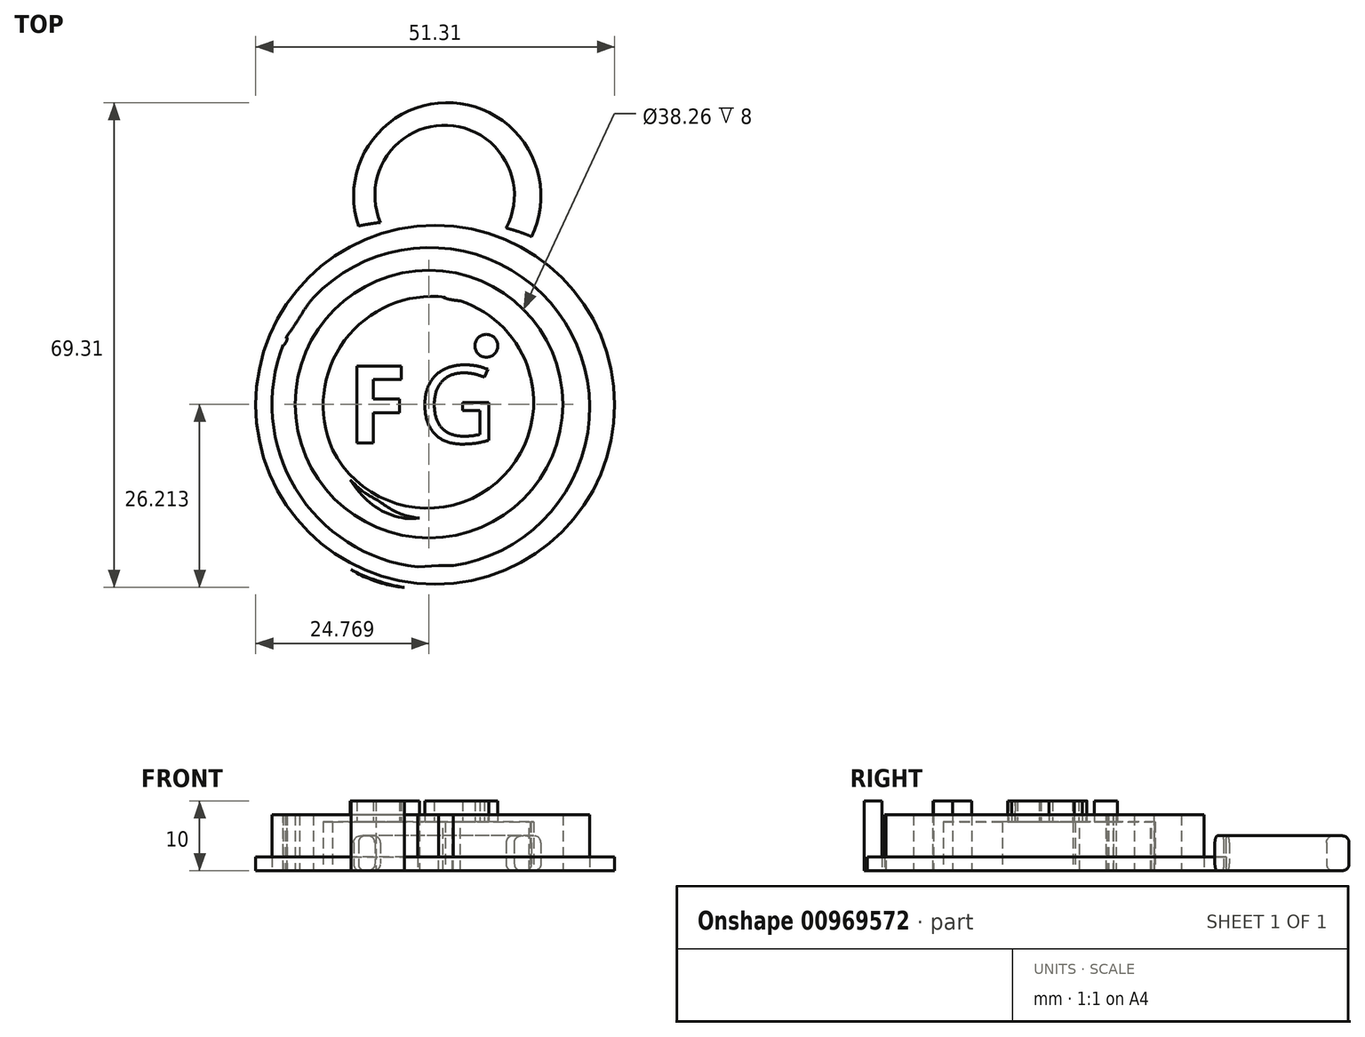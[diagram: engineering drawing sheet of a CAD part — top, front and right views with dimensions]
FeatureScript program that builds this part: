
annotation { "Feature Type Name" : "Feature", "Feature Type Description" : "" }
export const myFeature = defineFeature(function(context is Context, id is Id, definition is map)
    precondition{}
    {
        {
            var Q0;
            Q0=qCreatedBy(makeId("Top.planeOp"),FACE);
            var sketch = newSketch(context, id + "F0", { "sketchPlane" : qUnion([Q0])});
            skLineSegment(sketch, "E0", {"start": v(-44.03, -23.25) * mm, "end": v(-47.07, -23.48) * mm});
            skLineSegment(sketch, "E1", {"start": v(-47.07, -23.48) * mm, "end": v(-43.76, -23.38) * mm});
            skLineSegment(sketch, "E2", {"start": v(-0.42, -4.93) * mm, "end": v(0.75, -6.1) * mm});
            skLineSegment(sketch, "E3", {"start": v(0.75, -6.1) * mm, "end": v(0.2, -6.66) * mm});
            skLineSegment(sketch, "E4", {"start": v(0.2, -6.66) * mm, "end": v(-0.35, -7.2) * mm});
            skLineSegment(sketch, "E5", {"start": v(-0.35, -7.2) * mm, "end": v(-1.3, -6.23) * mm});
            skLineSegment(sketch, "E6", {"start": v(-5.27, -11.6) * mm, "end": v(-5.27, -10.95) * mm});
            skLineSegment(sketch, "E7", {"start": v(-5.27, -10.95) * mm, "end": v(-1.83, -10.95) * mm});
            skLineSegment(sketch, "E8", {"start": v(-1.83, -10.95) * mm, "end": v(1.61, -10.95) * mm});
            skLineSegment(sketch, "E9", {"start": v(1.61, -10.95) * mm, "end": v(1.53, -12.4) * mm});
            skLineSegment(sketch, "E10", {"start": v(34.95, -9.23) * mm, "end": v(34.95, -3.27) * mm});
            skLineSegment(sketch, "E11", {"start": v(34.95, -3.27) * mm, "end": v(35.66, -3.2) * mm});
            skLineSegment(sketch, "E12", {"start": v(35.66, -3.2) * mm, "end": v(36.37, -3.1) * mm});
            skLineSegment(sketch, "E13", {"start": v(36.37, -3.1) * mm, "end": v(36.45, -9.14) * mm});
            skLineSegment(sketch, "E14", {"start": v(44.6, -9.4) * mm, "end": v(44.74, -3.27) * mm});
            skLineSegment(sketch, "E15", {"start": v(44.74, -3.27) * mm, "end": v(45.47, -3.19) * mm});
            skLineSegment(sketch, "E16", {"start": v(45.47, -3.19) * mm, "end": v(46.2, -3.1) * mm});
            skLineSegment(sketch, "E17", {"start": v(46.2, -3.1) * mm, "end": v(46.18, -9.01) * mm});
            skLineSegment(sketch, "E18", {"start": v(4.45, -10.68) * mm, "end": v(4.52, -3.27) * mm});
            skLineSegment(sketch, "E19", {"start": v(4.52, -3.27) * mm, "end": v(5.85, -3.19) * mm});
            skLineSegment(sketch, "E20", {"start": v(9.42, -11.31) * mm, "end": v(8.63, -11.48) * mm});
            skLineSegment(sketch, "E21", {"start": v(8.63, -11.48) * mm, "end": v(11.3, -15.05) * mm});
            skLineSegment(sketch, "E22", {"start": v(11.3, -15.05) * mm, "end": v(13.95, -18.62) * mm});
            skLineSegment(sketch, "E23", {"start": v(13.95, -18.62) * mm, "end": v(13.08, -18.7) * mm});
            skLineSegment(sketch, "E24", {"start": v(5.98, -15.05) * mm, "end": v(5.98, -18.75) * mm});
            skLineSegment(sketch, "E25", {"start": v(5.98, -18.75) * mm, "end": v(5.3, -18.75) * mm});
            skLineSegment(sketch, "E26", {"start": v(7.18, -4.46) * mm, "end": v(5.98, -4.46) * mm});
            skLineSegment(sketch, "E27", {"start": v(5.98, -4.46) * mm, "end": v(5.98, -7.27) * mm});
            skLineSegment(sketch, "E28", {"start": v(5.98, -7.27) * mm, "end": v(5.98, -10.08) * mm});
            skLineSegment(sketch, "E29", {"start": v(5.98, -10.08) * mm, "end": v(7.86, -9.97) * mm});
            skLineSegment(sketch, "E30", {"start": v(49.96, -11.01) * mm, "end": v(50.03, -3.27) * mm});
            skLineSegment(sketch, "E31", {"start": v(50.03, -3.27) * mm, "end": v(51.62, -3.19) * mm});
            skLineSegment(sketch, "E32", {"start": v(52.88, -11.87) * mm, "end": v(51.49, -11.87) * mm});
            skLineSegment(sketch, "E33", {"start": v(51.49, -11.87) * mm, "end": v(51.49, -15.31) * mm});
            skLineSegment(sketch, "E34", {"start": v(51.49, -15.31) * mm, "end": v(51.49, -18.75) * mm});
            skLineSegment(sketch, "E35", {"start": v(51.49, -18.75) * mm, "end": v(50.69, -18.75) * mm});
            skLineSegment(sketch, "E36", {"start": v(50.69, -18.75) * mm, "end": v(49.9, -18.75) * mm});
            skLineSegment(sketch, "E37", {"start": v(49.9, -18.75) * mm, "end": v(49.96, -11.01) * mm});
            skLineSegment(sketch, "E38", {"start": v(52.61, -4.47) * mm, "end": v(51.49, -4.46) * mm});
            skLineSegment(sketch, "E39", {"start": v(51.49, -4.46) * mm, "end": v(51.49, -7.5) * mm});
            skLineSegment(sketch, "E40", {"start": v(-2.62, 13.4) * mm, "end": v(-2.62, 19.22) * mm});
            skLineSegment(sketch, "E41", {"start": v(-2.62, 19.22) * mm, "end": v(-1.38, 19.3) * mm});
            skLineSegment(sketch, "E42", {"start": v(-1.38, 19.3) * mm, "end": v(-0.14, 19.38) * mm});
            skLineSegment(sketch, "E43", {"start": v(-0.14, 19.38) * mm, "end": v(-0.06, 13.74) * mm});
            skLineSegment(sketch, "E44", {"start": v(7.57, 13.53) * mm, "end": v(7.7, 19.22) * mm});
            skLineSegment(sketch, "E45", {"start": v(7.7, 19.22) * mm, "end": v(8.89, 19.22) * mm});
            skLineSegment(sketch, "E46", {"start": v(8.89, 19.22) * mm, "end": v(10.08, 19.22) * mm});
            skLineSegment(sketch, "E47", {"start": v(10.08, 19.22) * mm, "end": v(10.08, 13.4) * mm});
            skLineSegment(sketch, "E48", {"start": v(1.1, 3.6) * mm, "end": v(1.1, 3.6) * mm});
            skLineSegment(sketch, "E49", {"start": v(22.7, 13.81) * mm, "end": v(22.78, 19.22) * mm});
            skLineSegment(sketch, "E50", {"start": v(22.78, 19.22) * mm, "end": v(23.97, 19.22) * mm});
            skLineSegment(sketch, "E51", {"start": v(23.97, 19.22) * mm, "end": v(25.16, 19.22) * mm});
            skLineSegment(sketch, "E52", {"start": v(25.16, 19.22) * mm, "end": v(25.3, 13.53) * mm});
            skLineSegment(sketch, "E53", {"start": v(32.92, 13.86) * mm, "end": v(33.01, 19.35) * mm});
            skLineSegment(sketch, "E54", {"start": v(33.01, 19.35) * mm, "end": v(34.18, 19.35) * mm});
            skLineSegment(sketch, "E55", {"start": v(34.18, 19.35) * mm, "end": v(35.35, 19.35) * mm});
            skLineSegment(sketch, "E56", {"start": v(35.35, 19.35) * mm, "end": v(35.35, 13.32) * mm});
            skLineSegment(sketch, "E57", {"start": v(-13.27, 11.48) * mm, "end": v(-13.2, 19.22) * mm});
            skLineSegment(sketch, "E58", {"start": v(-13.2, 19.22) * mm, "end": v(-8.97, 19.22) * mm});
            skLineSegment(sketch, "E59", {"start": v(-8.97, 19.22) * mm, "end": v(-4.74, 19.22) * mm});
            skLineSegment(sketch, "E60", {"start": v(-4.74, 19.22) * mm, "end": v(-4.66, 18.1) * mm});
            skLineSegment(sketch, "E61", {"start": v(-4.66, 18.1) * mm, "end": v(-4.57, 16.97) * mm});
            skLineSegment(sketch, "E62", {"start": v(-4.57, 16.97) * mm, "end": v(-7.63, 16.97) * mm});
            skLineSegment(sketch, "E63", {"start": v(-7.63, 16.97) * mm, "end": v(-10.69, 16.97) * mm});
            skLineSegment(sketch, "E64", {"start": v(-10.69, 16.97) * mm, "end": v(-10.69, 15.12) * mm});
            skLineSegment(sketch, "E65", {"start": v(-10.69, 15.12) * mm, "end": v(-10.69, 13.26) * mm});
            skLineSegment(sketch, "E66", {"start": v(-10.69, 13.26) * mm, "end": v(-7.65, 13.26) * mm});
            skLineSegment(sketch, "E67", {"start": v(-7.65, 13.26) * mm, "end": v(-4.6, 13.26) * mm});
            skLineSegment(sketch, "E68", {"start": v(-4.6, 13.26) * mm, "end": v(-4.6, 12.07) * mm});
            skLineSegment(sketch, "E69", {"start": v(-4.6, 12.07) * mm, "end": v(-4.6, 10.88) * mm});
            skLineSegment(sketch, "E70", {"start": v(-4.6, 10.88) * mm, "end": v(-7.65, 10.88) * mm});
            skLineSegment(sketch, "E71", {"start": v(-7.65, 10.88) * mm, "end": v(-10.69, 10.88) * mm});
            skLineSegment(sketch, "E72", {"start": v(-10.69, 10.88) * mm, "end": v(-10.69, 7.31) * mm});
            skLineSegment(sketch, "E73", {"start": v(-10.69, 7.31) * mm, "end": v(-10.69, 3.74) * mm});
            skLineSegment(sketch, "E74", {"start": v(-10.69, 3.74) * mm, "end": v(-12.02, 3.74) * mm});
            skLineSegment(sketch, "E75", {"start": v(-12.02, 3.74) * mm, "end": v(-13.34, 3.74) * mm});
            skLineSegment(sketch, "E76", {"start": v(-13.34, 3.74) * mm, "end": v(-13.27, 11.48) * mm});
            skLineSegment(sketch, "E77", {"start": v(14.99, 10.29) * mm, "end": v(15.01, 16.84) * mm});
            skLineSegment(sketch, "E78", {"start": v(15.01, 16.84) * mm, "end": v(13, 16.91) * mm});
            skLineSegment(sketch, "E79", {"start": v(13, 16.91) * mm, "end": v(10.98, 17) * mm});
            skLineSegment(sketch, "E80", {"start": v(10.98, 17) * mm, "end": v(11.06, 18.1) * mm});
            skLineSegment(sketch, "E81", {"start": v(11.06, 18.1) * mm, "end": v(11.14, 19.22) * mm});
            skLineSegment(sketch, "E82", {"start": v(11.14, 19.22) * mm, "end": v(16.43, 19.22) * mm});
            skLineSegment(sketch, "E83", {"start": v(16.43, 19.22) * mm, "end": v(21.72, 19.22) * mm});
            skLineSegment(sketch, "E84", {"start": v(21.72, 19.22) * mm, "end": v(21.8, 18.1) * mm});
            skLineSegment(sketch, "E85", {"start": v(21.8, 18.1) * mm, "end": v(21.88, 17) * mm});
            skLineSegment(sketch, "E86", {"start": v(21.88, 17) * mm, "end": v(19.82, 16.91) * mm});
            skLineSegment(sketch, "E87", {"start": v(19.82, 16.91) * mm, "end": v(17.75, 16.84) * mm});
            skLineSegment(sketch, "E88", {"start": v(17.75, 16.84) * mm, "end": v(17.75, 10.29) * mm});
            skLineSegment(sketch, "E89", {"start": v(17.75, 10.29) * mm, "end": v(17.75, 3.74) * mm});
            skLineSegment(sketch, "E90", {"start": v(17.75, 3.74) * mm, "end": v(16.36, 3.74) * mm});
            skLineSegment(sketch, "E91", {"start": v(16.36, 3.74) * mm, "end": v(14.96, 3.74) * mm});
            skLineSegment(sketch, "E92", {"start": v(14.96, 3.74) * mm, "end": v(14.99, 10.29) * mm});
            skLineSegment(sketch, "E93", {"start": v(38.06, 11.48) * mm, "end": v(38.13, 19.22) * mm});
            skLineSegment(sketch, "E94", {"start": v(38.13, 19.22) * mm, "end": v(41.1, 19.18) * mm});
            skLineSegment(sketch, "E95", {"start": v(44.73, 11.04) * mm, "end": v(43.66, 10.55) * mm});
            skLineSegment(sketch, "E96", {"start": v(43.66, 10.55) * mm, "end": v(46.05, 7.29) * mm});
            skLineSegment(sketch, "E97", {"start": v(63.29, 4.6) * mm, "end": v(63.67, 3.74) * mm});
            skLineSegment(sketch, "E98", {"start": v(63.67, 3.74) * mm, "end": v(62.27, 3.74) * mm});
            skLineSegment(sketch, "E99", {"start": v(62.27, 3.74) * mm, "end": v(60.88, 3.74) * mm});
            skLineSegment(sketch, "E100", {"start": v(60.88, 3.74) * mm, "end": v(60.06, 5.66) * mm});
            skLineSegment(sketch, "E101", {"start": v(60.06, 5.66) * mm, "end": v(59.24, 7.57) * mm});
            skLineSegment(sketch, "E102", {"start": v(59.24, 7.57) * mm, "end": v(56.22, 7.57) * mm});
            skLineSegment(sketch, "E103", {"start": v(56.22, 7.57) * mm, "end": v(53.2, 7.57) * mm});
            skLineSegment(sketch, "E104", {"start": v(53.2, 7.57) * mm, "end": v(52.75, 6.66) * mm});
            skLineSegment(sketch, "E105", {"start": v(51.9, 4.74) * mm, "end": v(51.5, 3.74) * mm});
            skLineSegment(sketch, "E106", {"start": v(51.5, 3.74) * mm, "end": v(48.6, 3.74) * mm});
            skLineSegment(sketch, "E107", {"start": v(48.6, 3.74) * mm, "end": v(45.7, 3.74) * mm});
            skLineSegment(sketch, "E108", {"start": v(45.7, 3.74) * mm, "end": v(43.43, 6.9) * mm});
            skLineSegment(sketch, "E109", {"start": v(40.64, 7.06) * mm, "end": v(40.64, 3.74) * mm});
            skLineSegment(sketch, "E110", {"start": v(40.64, 3.74) * mm, "end": v(39.31, 3.74) * mm});
            skLineSegment(sketch, "E111", {"start": v(39.31, 3.74) * mm, "end": v(37.99, 3.74) * mm});
            skLineSegment(sketch, "E112", {"start": v(37.99, 3.74) * mm, "end": v(38.06, 11.48) * mm});
            skLineSegment(sketch, "E113", {"start": v(42.1, 16.79) * mm, "end": v(40.77, 16.84) * mm});
            skLineSegment(sketch, "E114", {"start": v(40.77, 16.84) * mm, "end": v(40.7, 14.78) * mm});
            skLineSegment(sketch, "E115", {"start": v(40.7, 14.78) * mm, "end": v(40.62, 12.73) * mm});
            skLineSegment(sketch, "E116", {"start": v(40.62, 12.73) * mm, "end": v(41.95, 12.73) * mm});
            skFitSpline(sketch, "E117", {"points": [v(-48.97, -26.41) * mm, v(-51.63, -25.94) * mm, v(-55.3, -24.57) * mm, v(-57.59, -23.21) * mm]});
            skFitSpline(sketch, "E118", {"points": [v(-57.59, -23.21) * mm, v(-63.3, -19.81) * mm, v(-66.86, -15.56) * mm, v(-69.4, -9.15) * mm]});
            skFitSpline(sketch, "E119", {"points": [v(-69.4, -9.15) * mm, v(-71.48, -3.92) * mm, v(-71.54, 3.34) * mm, v(-69.55, 8.65) * mm]});
            skFitSpline(sketch, "E120", {"points": [v(-69.56, 8.67) * mm, v(-66.12, 17.83) * mm, v(-58.94, 24.16) * mm, v(-49.87, 26.04) * mm]});
            skFitSpline(sketch, "E121", {"points": [v(-49.86, 26.02) * mm, v(-46.19, 26.78) * mm, v(-40.37, 26.59) * mm, v(-37.07, 25.6) * mm]});
            skFitSpline(sketch, "E122", {"points": [v(-37.07, 25.6) * mm, v(-30.64, 23.67) * mm, v(-25.03, 19.32) * mm, v(-21.64, 13.64) * mm]});
            skFitSpline(sketch, "E123", {"points": [v(-21.64, 13.64) * mm, v(-17.98, 7.51) * mm, v(-16.93, 0.08) * mm, v(-18.72, -6.9) * mm]});
            skFitSpline(sketch, "E124", {"points": [v(-18.72, -6.9) * mm, v(-21.07, -16.02) * mm, v(-28.59, -23.55) * mm, v(-37.68, -25.92) * mm]});
            skFitSpline(sketch, "E125", {"points": [v(-37.68, -25.92) * mm, v(-40.2, -26.57) * mm, v(-46.51, -26.85) * mm, v(-48.97, -26.41) * mm]});
            skFitSpline(sketch, "E126", {"points": [v(-38.2, -22.63) * mm, v(-35.14, -21.72) * mm, v(-33.7, -21.08) * mm, v(-31.51, -19.6) * mm]});
            skFitSpline(sketch, "E127", {"points": [v(-31.51, -19.6) * mm, v(-26.64, -16.35) * mm, v(-23.18, -11.38) * mm, v(-21.75, -5.6) * mm]});
            skFitSpline(sketch, "E128", {"points": [v(-21.75, -5.6) * mm, v(-20.9, -2.13) * mm, v(-20.94, 2.46) * mm, v(-21.88, 5.9) * mm]});
            skFitSpline(sketch, "E129", {"points": [v(-21.88, 5.9) * mm, v(-23.68, 12.54) * mm, v(-28.15, 18.04) * mm, v(-34.12, 20.95) * mm]});
            skFitSpline(sketch, "E130", {"points": [v(-34.12, 20.95) * mm, v(-39.89, 23.76) * mm, v(-46.96, 24.05) * mm, v(-53.02, 21.71) * mm]});
            skFitSpline(sketch, "E131", {"points": [v(-53.02, 21.71) * mm, v(-57.82, 19.87) * mm, v(-62.76, 15.41) * mm, v(-65.06, 10.88) * mm]});
            skFitSpline(sketch, "E132", {"points": [v(-65.06, 10.88) * mm, v(-65.7, 9.62) * mm, v(-65.47, 9.88) * mm, v(-63.9, 12.23) * mm]});
            skFitSpline(sketch, "E133", {"points": [v(-63.9, 12.23) * mm, v(-62.4, 14.5) * mm, v(-59.48, 17.39) * mm, v(-57.14, 18.93) * mm]});
            skFitSpline(sketch, "E134", {"points": [v(-57.14, 18.93) * mm, v(-55.36, 20.11) * mm, v(-52.56, 21.26) * mm, v(-49.92, 21.9) * mm]});
            skFitSpline(sketch, "E135", {"points": [v(-49.92, 21.9) * mm, v(-47.26, 22.55) * mm, v(-42.13, 22.48) * mm, v(-39.4, 21.75) * mm]});
            skFitSpline(sketch, "E136", {"points": [v(-39.4, 21.75) * mm, v(-31.8, 19.74) * mm, v(-25.84, 14.14) * mm, v(-23.33, 6.65) * mm]});
            skFitSpline(sketch, "E137", {"points": [v(-23.33, 6.65) * mm, v(-22.52, 4.24) * mm, v(-22.49, 3.96) * mm, v(-22.48, -0.23) * mm]});
            skFitSpline(sketch, "E138", {"points": [v(-22.48, -0.23) * mm, v(-22.46, -5.24) * mm, v(-22.86, -7.13) * mm, v(-24.7, -10.8) * mm]});
            skFitSpline(sketch, "E139", {"points": [v(-24.7, -10.8) * mm, v(-28.37, -18.09) * mm, v(-35.4, -22.62) * mm, v(-44.03, -23.25) * mm]});
            skFitSpline(sketch, "E140", {"points": [v(-43.76, -23.38) * mm, v(-41.2, -23.31) * mm, v(-39.94, -23.14) * mm, v(-38.2, -22.63) * mm]});
            skFitSpline(sketch, "E141", {"points": [v(-41.15, -15.54) * mm, v(-37.63, -14.7) * mm, v(-33.69, -11.85) * mm, v(-31.89, -8.86) * mm]});
            skFitSpline(sketch, "E142", {"points": [v(-31.89, -8.86) * mm, v(-30.14, -5.94) * mm, v(-29.65, -4.17) * mm, v(-29.63, -0.63) * mm]});
            skFitSpline(sketch, "E143", {"points": [v(-29.63, -0.63) * mm, v(-29.61, 2.06) * mm, v(-29.7, 2.85) * mm, v(-30.25, 4.52) * mm]});
            skFitSpline(sketch, "E144", {"points": [v(-30.25, 4.52) * mm, v(-31.54, 8.44) * mm, v(-34.55, 11.9) * mm, v(-38.14, 13.6) * mm]});
            skFitSpline(sketch, "E145", {"points": [v(-38.14, 13.6) * mm, v(-39.89, 14.42) * mm, v(-42.23, 15.12) * mm, v(-43.1, 15.1) * mm]});
            skFitSpline(sketch, "E146", {"points": [v(-43.1, 15.1) * mm, v(-43.4, 15.08) * mm, v(-42.93, 14.9) * mm, v(-42.08, 14.7) * mm]});
            skFitSpline(sketch, "E147", {"points": [v(-42.08, 14.7) * mm, v(-36.92, 13.45) * mm, v(-32.57, 9.17) * mm, v(-30.96, 3.76) * mm]});
            skFitSpline(sketch, "E148", {"points": [v(-30.96, 3.76) * mm, v(-30.42, 1.93) * mm, v(-30.4, -1.75) * mm, v(-30.94, -3.79) * mm]});
            skFitSpline(sketch, "E149", {"points": [v(-30.94, -3.79) * mm, v(-31.46, -5.77) * mm, v(-32.89, -8.48) * mm, v(-34.25, -10.07) * mm]});
            skFitSpline(sketch, "E150", {"points": [v(-34.25, -10.07) * mm, v(-35.7, -11.76) * mm, v(-38.9, -13.86) * mm, v(-41.05, -14.52) * mm]});
            skFitSpline(sketch, "E151", {"points": [v(-41.05, -14.52) * mm, v(-47.68, -16.57) * mm, v(-53.9, -14.29) * mm, v(-58.4, -8.15) * mm]});
            skFitSpline(sketch, "E152", {"points": [v(-58.4, -8.15) * mm, v(-58.85, -7.53) * mm, v(-58.85, -7.54) * mm, v(-58.4, -8.41) * mm]});
            skFitSpline(sketch, "E153", {"points": [v(-58.4, -8.41) * mm, v(-57.6, -9.92) * mm, v(-54.78, -12.73) * mm, v(-52.99, -13.8) * mm]});
            skFitSpline(sketch, "E154", {"points": [v(-52.99, -13.8) * mm, v(-49.48, -15.88) * mm, v(-45.2, -16.5) * mm, v(-41.15, -15.54) * mm]});
            skFitSpline(sketch, "E155", {"points": [v(-65.73, 9.16) * mm, v(-65.73, 9.3) * mm, v(-65.85, 9.25) * mm, v(-65.99, 9.03) * mm]});
            skFitSpline(sketch, "E156", {"points": [v(-65.99, 9.03) * mm, v(-66.13, 8.81) * mm, v(-66.24, 8.51) * mm, v(-66.24, 8.37) * mm]});
            skFitSpline(sketch, "E157", {"points": [v(-66.24, 8.37) * mm, v(-66.24, 8.22) * mm, v(-66.13, 8.28) * mm, v(-65.99, 8.5) * mm]});
            skFitSpline(sketch, "E158", {"points": [v(-65.99, 8.5) * mm, v(-65.85, 8.72) * mm, v(-65.73, 9.02) * mm, v(-65.73, 9.16) * mm]});
            skFitSpline(sketch, "E159", {"points": [v(-7.85, -19) * mm, v(-10.55, -18.33) * mm, v(-12.78, -16.26) * mm, v(-13.5, -13.77) * mm]});
            skFitSpline(sketch, "E160", {"points": [v(-13.5, -13.77) * mm, v(-14.05, -11.9) * mm, v(-13.89, -9) * mm, v(-13.15, -7.37) * mm]});
            skFitSpline(sketch, "E161", {"points": [v(-13.15, -7.37) * mm, v(-11.9, -4.6) * mm, v(-9.18, -2.88) * mm, v(-6.04, -2.88) * mm]});
            skFitSpline(sketch, "E162", {"points": [v(-6.04, -2.88) * mm, v(-3.52, -2.88) * mm, v(-1.87, -3.48) * mm, v(-0.42, -4.93) * mm]});
            skFitSpline(sketch, "E163", {"points": [v(-1.3, -6.23) * mm, v(-2.48, -5.02) * mm, v(-3.34, -4.57) * mm, v(-4.93, -4.33) * mm]});
            skFitSpline(sketch, "E164", {"points": [v(-4.93, -4.33) * mm, v(-6.78, -4.05) * mm, v(-8.6, -4.58) * mm, v(-10, -5.82) * mm]});
            skFitSpline(sketch, "E165", {"points": [v(-10, -5.82) * mm, v(-11.52, -7.15) * mm, v(-12.15, -8.75) * mm, v(-12.13, -11.22) * mm]});
            skFitSpline(sketch, "E166", {"points": [v(-12.13, -11.22) * mm, v(-12.11, -14.87) * mm, v(-9.8, -17.42) * mm, v(-6.32, -17.65) * mm]});
            skFitSpline(sketch, "E167", {"points": [v(-6.32, -17.65) * mm, v(-4.4, -17.77) * mm, v(-3.08, -17.4) * mm, v(-1.91, -16.42) * mm]});
            skFitSpline(sketch, "E168", {"points": [v(-1.91, -16.42) * mm, v(-1.03, -15.68) * mm, v(-0.12, -13.96) * mm, v(-0.11, -13) * mm]});
            skFitSpline(sketch, "E169", {"points": [v(-0.11, -13) * mm, v(-0.1, -12.45) * mm, v(-0.22, -12.42) * mm, v(-2.69, -12.34) * mm]});
            skFitSpline(sketch, "E170", {"points": [v(-2.69, -12.34) * mm, v(-5.24, -12.27) * mm, v(-5.27, -12.26) * mm, v(-5.27, -11.6) * mm]});
            skFitSpline(sketch, "E171", {"points": [v(1.53, -12.4) * mm, v(1.39, -15.08) * mm, v(0, -17.2) * mm, v(-2.3, -18.34) * mm]});
            skFitSpline(sketch, "E172", {"points": [v(-2.3, -18.34) * mm, v(-3.85, -19.1) * mm, v(-6.31, -19.4) * mm, v(-7.85, -19) * mm]});
            skFitSpline(sketch, "E173", {"points": [v(21.57, -18.93) * mm, v(19.9, -18.46) * mm, v(18.03, -17.32) * mm, v(17.26, -16.3) * mm]});
            skFitSpline(sketch, "E174", {"points": [v(17.26, -16.3) * mm, v(15.86, -14.42) * mm, v(15.4, -13.16) * mm, v(15.39, -11.08) * mm]});
            skFitSpline(sketch, "E175", {"points": [v(15.39, -11.08) * mm, v(15.36, -7.62) * mm, v(16.98, -5.1) * mm, v(20.2, -3.6) * mm]});
            skFitSpline(sketch, "E176", {"points": [v(20.2, -3.6) * mm, v(21.7, -2.9) * mm, v(22.08, -2.83) * mm, v(23.91, -2.93) * mm]});
            skFitSpline(sketch, "E177", {"points": [v(23.91, -2.93) * mm, v(26.33, -3.06) * mm, v(27.95, -3.74) * mm, v(29.5, -5.3) * mm]});
            skFitSpline(sketch, "E178", {"points": [v(29.5, -5.3) * mm, v(33.43, -9.22) * mm, v(32.34, -15.77) * mm, v(27.36, -18.2) * mm]});
            skFitSpline(sketch, "E179", {"points": [v(27.36, -18.2) * mm, v(25.4, -19.15) * mm, v(23.3, -19.42) * mm, v(21.57, -18.93) * mm]});
            skFitSpline(sketch, "E180", {"points": [v(26.82, -16.89) * mm, v(29.99, -15.07) * mm, v(31.18, -11.15) * mm, v(29.54, -7.93) * mm]});
            skFitSpline(sketch, "E181", {"points": [v(29.54, -7.93) * mm, v(28.86, -6.6) * mm, v(26.92, -4.9) * mm, v(25.6, -4.51) * mm]});
            skFitSpline(sketch, "E182", {"points": [v(25.6, -4.51) * mm, v(23.3, -3.82) * mm, v(21.1, -4.29) * mm, v(19.31, -5.87) * mm]});
            skFitSpline(sketch, "E183", {"points": [v(19.31, -5.87) * mm, v(17.15, -7.77) * mm, v(16.4, -10.27) * mm, v(17.18, -12.96) * mm]});
            skFitSpline(sketch, "E184", {"points": [v(17.18, -12.96) * mm, v(18.05, -15.95) * mm, v(20.37, -17.66) * mm, v(23.57, -17.68) * mm]});
            skFitSpline(sketch, "E185", {"points": [v(23.57, -17.68) * mm, v(25.16, -17.69) * mm, v(25.62, -17.57) * mm, v(26.82, -16.89) * mm]});
            skFitSpline(sketch, "E186", {"points": [v(38.88, -19.04) * mm, v(37.4, -18.66) * mm, v(36.2, -17.73) * mm, v(35.56, -16.43) * mm]});
            skFitSpline(sketch, "E187", {"points": [v(35.56, -16.43) * mm, v(34.98, -15.23) * mm, v(34.95, -14.92) * mm, v(34.95, -9.23) * mm]});
            skFitSpline(sketch, "E188", {"points": [v(36.45, -9.14) * mm, v(36.53, -14.3) * mm, v(36.6, -15.3) * mm, v(37, -16.03) * mm]});
            skFitSpline(sketch, "E189", {"points": [v(37, -16.03) * mm, v(37.64, -17.2) * mm, v(38.72, -17.7) * mm, v(40.56, -17.69) * mm]});
            skFitSpline(sketch, "E190", {"points": [v(40.56, -17.69) * mm, v(42.32, -17.68) * mm, v(43.13, -17.34) * mm, v(43.92, -16.29) * mm]});
            skFitSpline(sketch, "E191", {"points": [v(43.92, -16.29) * mm, v(44.44, -15.6) * mm, v(44.49, -15.1) * mm, v(44.6, -9.4) * mm]});
            skFitSpline(sketch, "E192", {"points": [v(46.18, -9.01) * mm, v(46.17, -15.16) * mm, v(46, -16.32) * mm, v(44.96, -17.47) * mm]});
            skFitSpline(sketch, "E193", {"points": [v(44.96, -17.47) * mm, v(43.8, -18.77) * mm, v(40.82, -19.54) * mm, v(38.88, -19.04) * mm]});
            skFitSpline(sketch, "E194", {"points": [v(4.51, -18.42) * mm, v(4.44, -18.23) * mm, v(4.41, -14.75) * mm, v(4.45, -10.68) * mm]});
            skFitSpline(sketch, "E195", {"points": [v(5.85, -3.19) * mm, v(9, -2.98) * mm, v(11.26, -3.77) * mm, v(12.01, -5.33) * mm]});
            skFitSpline(sketch, "E196", {"points": [v(12.01, -5.33) * mm, v(12.5, -6.34) * mm, v(12.46, -8.46) * mm, v(11.95, -9.45) * mm]});
            skFitSpline(sketch, "E197", {"points": [v(11.95, -9.45) * mm, v(11.46, -10.4) * mm, v(10.54, -11.08) * mm, v(9.42, -11.31) * mm]});
            skFitSpline(sketch, "E198", {"points": [v(13.08, -18.7) * mm, v(12.48, -18.77) * mm, v(12.12, -18.65) * mm, v(11.87, -18.3) * mm]});
            skFitSpline(sketch, "E199", {"points": [v(11.87, -18.3) * mm, v(8.9, -14.16) * mm, v(6.68, -11.34) * mm, v(6.37, -11.34) * mm]});
            skFitSpline(sketch, "E200", {"points": [v(6.37, -11.34) * mm, v(6.04, -11.34) * mm, v(5.98, -11.98) * mm, v(5.98, -15.05) * mm]});
            skFitSpline(sketch, "E201", {"points": [v(5.3, -18.75) * mm, v(4.94, -18.75) * mm, v(4.58, -18.6) * mm, v(4.51, -18.42) * mm]});
            skFitSpline(sketch, "E202", {"points": [v(10.24, -9.25) * mm, v(10.8, -8.56) * mm, v(10.92, -6.62) * mm, v(10.46, -5.75) * mm]});
            skFitSpline(sketch, "E203", {"points": [v(10.46, -5.75) * mm, v(10.07, -5.02) * mm, v(8.64, -4.46) * mm, v(7.18, -4.46) * mm]});
            skFitSpline(sketch, "E204", {"points": [v(7.86, -9.97) * mm, v(9.44, -9.88) * mm, v(9.83, -9.77) * mm, v(10.24, -9.25) * mm]});
            skFitSpline(sketch, "E205", {"points": [v(51.62, -3.19) * mm, v(52.5, -3.14) * mm, v(53.86, -3.18) * mm, v(54.66, -3.28) * mm]});
            skFitSpline(sketch, "E206", {"points": [v(54.66, -3.28) * mm, v(55.9, -3.43) * mm, v(56.27, -3.62) * mm, v(57.1, -4.48) * mm]});
            skFitSpline(sketch, "E207", {"points": [v(57.1, -4.48) * mm, v(58.22, -5.67) * mm, v(58.58, -7.19) * mm, v(58.13, -8.86) * mm]});
            skFitSpline(sketch, "E208", {"points": [v(58.13, -8.86) * mm, v(57.6, -10.84) * mm, v(55.8, -11.87) * mm, v(52.88, -11.87) * mm]});
            skFitSpline(sketch, "E209", {"points": [v(53.99, -10.29) * mm, v(56.05, -9.95) * mm, v(56.62, -9.39) * mm, v(56.62, -7.68) * mm]});
            skFitSpline(sketch, "E210", {"points": [v(56.62, -7.68) * mm, v(56.62, -5.4) * mm, v(55.44, -4.47) * mm, v(52.61, -4.47) * mm]});
            skFitSpline(sketch, "E211", {"points": [v(51.49, -7.5) * mm, v(51.49, -10.96) * mm, v(51.28, -10.73) * mm, v(53.99, -10.29) * mm]});
            skFitSpline(sketch, "E212", {"points": [v(1.1, 3.6) * mm, v(-0.47, 4.16) * mm, v(-1.23, 4.82) * mm, v(-1.96, 6.27) * mm]});
            skFitSpline(sketch, "E213", {"points": [v(-1.96, 6.27) * mm, v(-2.6, 7.54) * mm, v(-2.62, 7.71) * mm, v(-2.62, 13.4) * mm]});
            skFitSpline(sketch, "E214", {"points": [v(-0.06, 13.74) * mm, v(0.04, 7.33) * mm, v(0.2, 6.74) * mm, v(2.07, 6) * mm]});
            skFitSpline(sketch, "E215", {"points": [v(2.07, 6) * mm, v(3.35, 5.48) * mm, v(4.12, 5.48) * mm, v(5.43, 6) * mm]});
            skFitSpline(sketch, "E216", {"points": [v(5.43, 6) * mm, v(7.32, 6.77) * mm, v(7.42, 7.1) * mm, v(7.57, 13.53) * mm]});
            skFitSpline(sketch, "E217", {"points": [v(10.08, 13.4) * mm, v(10.08, 10.2) * mm, v(9.99, 7.24) * mm, v(9.87, 6.84) * mm]});
            skFitSpline(sketch, "E218", {"points": [v(9.87, 6.84) * mm, v(9.52, 5.55) * mm, v(7.9, 4.05) * mm, v(6.43, 3.6) * mm]});
            skFitSpline(sketch, "E219", {"points": [v(6.43, 3.6) * mm, v(4.77, 3.11) * mm, v(2.48, 3.11) * mm, v(1.1, 3.6) * mm]});
            skFitSpline(sketch, "E220", {"points": [v(26.38, 3.6) * mm, v(25.74, 3.8) * mm, v(24.82, 4.36) * mm, v(24.32, 4.84) * mm]});
            skFitSpline(sketch, "E221", {"points": [v(24.32, 4.84) * mm, v(22.86, 6.26) * mm, v(22.63, 7.56) * mm, v(22.7, 13.81) * mm]});
            skFitSpline(sketch, "E222", {"points": [v(25.3, 13.53) * mm, v(25.44, 7.04) * mm, v(25.53, 6.74) * mm, v(27.56, 5.97) * mm]});
            skFitSpline(sketch, "E223", {"points": [v(27.56, 5.97) * mm, v(28.92, 5.45) * mm, v(30.36, 5.59) * mm, v(31.37, 6.33) * mm]});
            skFitSpline(sketch, "E224", {"points": [v(31.37, 6.33) * mm, v(32.7, 7.31) * mm, v(32.83, 7.96) * mm, v(32.92, 13.86) * mm]});
            skFitSpline(sketch, "E225", {"points": [v(35.35, 13.32) * mm, v(35.35, 7.6) * mm, v(35.32, 7.23) * mm, v(34.75, 6.11) * mm]});
            skFitSpline(sketch, "E226", {"points": [v(34.75, 6.11) * mm, v(34.1, 4.83) * mm, v(32.92, 3.9) * mm, v(31.41, 3.48) * mm]});
            skFitSpline(sketch, "E227", {"points": [v(31.41, 3.48) * mm, v(30.1, 3.11) * mm, v(27.78, 3.17) * mm, v(26.38, 3.6) * mm]});
            skFitSpline(sketch, "E228", {"points": [v(41.1, 19.18) * mm, v(43.46, 19.15) * mm, v(44.23, 19.04) * mm, v(44.9, 18.65) * mm]});
            skFitSpline(sketch, "E229", {"points": [v(44.9, 18.65) * mm, v(46.28, 17.84) * mm, v(46.82, 16.9) * mm, v(46.93, 15.05) * mm]});
            skFitSpline(sketch, "E230", {"points": [v(46.93, 15.05) * mm, v(47.02, 13.65) * mm, v(46.94, 13.25) * mm, v(46.42, 12.47) * mm]});
            skFitSpline(sketch, "E231", {"points": [v(46.42, 12.47) * mm, v(46.08, 11.96) * mm, v(45.32, 11.32) * mm, v(44.73, 11.04) * mm]});
            skFitSpline(sketch, "E232", {"points": [v(46.05, 7.29) * mm, v(47.37, 5.5) * mm, v(48.5, 4.03) * mm, v(48.59, 4.02) * mm]});
            skFitSpline(sketch, "E233", {"points": [v(48.59, 4.02) * mm, v(48.78, 4) * mm, v(49.77, 6.01) * mm, v(52.54, 12.07) * mm]});
            skFitSpline(sketch, "E234", {"points": [v(52.54, 12.07) * mm, v(53.8, 14.84) * mm, v(55.14, 17.69) * mm, v(55.5, 18.4) * mm]});
            skFitSpline(sketch, "E235", {"points": [v(55.5, 18.4) * mm, v(56.18, 19.71) * mm, v(56.18, 19.71) * mm, v(56.52, 19.07) * mm]});
            skFitSpline(sketch, "E236", {"points": [v(56.52, 19.07) * mm, v(56.87, 18.43) * mm, v(62.55, 6.27) * mm, v(63.29, 4.6) * mm]});
            skFitSpline(sketch, "E237", {"points": [v(52.75, 6.66) * mm, v(52.5, 6.16) * mm, v(52.12, 5.3) * mm, v(51.9, 4.74) * mm]});
            skFitSpline(sketch, "E238", {"points": [v(43.43, 6.9) * mm, v(42.17, 8.64) * mm, v(41.04, 10.14) * mm, v(40.9, 10.23) * mm]});
            skFitSpline(sketch, "E239", {"points": [v(40.9, 10.23) * mm, v(40.74, 10.32) * mm, v(40.64, 9.14) * mm, v(40.64, 7.06) * mm]});
            skFitSpline(sketch, "E240", {"points": [v(58.1, 9.98) * mm, v(58.1, 10.06) * mm, v(57.76, 10.93) * mm, v(57.35, 11.9) * mm]});
            skFitSpline(sketch, "E241", {"points": [v(57.35, 11.9) * mm, v(56.93, 12.87) * mm, v(56.5, 13.9) * mm, v(56.4, 14.18) * mm]});
            skFitSpline(sketch, "E242", {"points": [v(56.4, 14.18) * mm, v(56.26, 14.58) * mm, v(56.01, 14.19) * mm, v(55.31, 12.46) * mm]});
            skFitSpline(sketch, "E243", {"points": [v(55.31, 12.46) * mm, v(54.82, 11.23) * mm, v(54.4, 10.13) * mm, v(54.4, 10.02) * mm]});
            skFitSpline(sketch, "E244", {"points": [v(54.4, 10.02) * mm, v(54.4, 9.91) * mm, v(55.23, 9.82) * mm, v(56.25, 9.82) * mm]});
            skFitSpline(sketch, "E245", {"points": [v(56.25, 9.82) * mm, v(57.27, 9.82) * mm, v(58.1, 9.9) * mm, v(58.1, 9.98) * mm]});
            skFitSpline(sketch, "E246", {"points": [v(43.81, 13.26) * mm, v(44.48, 13.93) * mm, v(44.5, 15.38) * mm, v(43.88, 16.16) * mm]});
            skFitSpline(sketch, "E247", {"points": [v(43.88, 16.16) * mm, v(43.52, 16.6) * mm, v(43.09, 16.75) * mm, v(42.1, 16.79) * mm]});
            skFitSpline(sketch, "E248", {"points": [v(41.95, 12.73) * mm, v(42.93, 12.73) * mm, v(43.43, 12.87) * mm, v(43.81, 13.26) * mm]});
            skFitSpline(sketch, "E249", {"points": [v(65.14, 19.6) * mm, v(61.89, 21.74) * mm, v(63.25, 26.62) * mm, v(67.1, 26.62) * mm]});
            skFitSpline(sketch, "E250", {"points": [v(67.1, 26.62) * mm, v(69.92, 26.62) * mm, v(71.89, 23.58) * mm, v(70.6, 21.2) * mm]});
            skFitSpline(sketch, "E251", {"points": [v(70.6, 21.2) * mm, v(69.5, 19.22) * mm, v(66.89, 18.44) * mm, v(65.14, 19.6) * mm]});
            skCircle(sketch, "E252", {"center": v(-45.65, 0.12) * mm, "radius": 15.19 * mm});
            skPoint(sketch, "E252.second.point", {"position": v(-32.39, -7.28) * mm});
            skCircle(sketch, "E253", {"center": v(-44.97, -0.39) * mm, "radius": 15.59 * mm});
            skPoint(sketch, "E253.third.point", {"position": v(-57.19, -10.07) * mm});
            skCircle(sketch, "E254", {"center": v(-45.43, -0.2) * mm, "radius": 19.13 * mm});
            skPoint(sketch, "E254.first.point", {"position": v(-52.66, 17.51) * mm});
            skPoint(sketch, "E254.second.point", {"position": v(-27.36, -6.45) * mm});
            skPoint(sketch, "E254.third.point", {"position": v(-50.49, -18.64) * mm});
            skCircle(sketch, "E255", {"center": v(-45.33, -0.68) * mm, "radius": 22.86 * mm});
            skCircle(sketch, "E256", {"center": v(-44.46, -0.22) * mm, "radius": 23.4 * mm});
            skCircle(sketch, "E257", {"center": v(-44.41, -0.17) * mm, "radius": 26.64 * mm});
            skArc(sketch, "E258", {"start": v(-31.16, 22.94) * mm, "mid": v(-42.04, 42.88) * mm, "end": v(-55.17, 24.35) * mm});
            skArc(sketch, "E259", {"start": v(-34.63, 24.6) * mm, "mid": v(-42.8, 39.66) * mm, "end": v(-52.15, 25.32) * mm});
            skSolve(sketch);
        }
        {
            var Q0;
            {var subQ12=sQuery(id+"F0.wireOp",EDGE,"E146");Q0=makeQuery(id+"F0.imprint","IMPRINT",FACE,{"disambiguationData":[TD([[makeQuery(id+"F0.imprint","IMPRINT",EDGE,{"derivedFrom":subQ12}),-1.0]])]});}
            extrude(context, id + "F1", {"entities" : qUnion([Q0]), "depth" : 7 * mm, "offsetDistance" : 25 * mm});
        }
        {
            var Q0;
            {var subQ11=sQuery(id+"F0.wireOp",EDGE,"E154");Q0=makeQuery(id+"F0.imprint","IMPRINT",FACE,{"disambiguationData":[TD([[makeQuery(id+"F0.imprint","IMPRINT",EDGE,{"derivedFrom":subQ11}),-1.0]])]});}
            extrude(context, id + "F2", {"entities" : qUnion([Q0]), "depth" : 10 * mm, "offsetDistance" : 25 * mm});
        }
        {
            var Q0;
            {var subQ6=sQuery(id+"F0.wireOp",EDGE,"E0");Q0=makeQuery(id+"F0.imprint","IMPRINT",FACE,{"disambiguationData":[TD([[makeQuery(id+"F0.imprint","IMPRINT",EDGE,{"derivedFrom":subQ6}),-1.0]])]});}
            extrude(context, id + "F3", {"entities" : qUnion([Q0]), "operationType" : NewBodyOperationType.ADD, "depth" : 8 * mm, "offsetDistance" : 25 * mm});
        }
        {
            var Q0;
            {var subQ7=sQuery(id+"F0.wireOp",EDGE,"E117");Q0=makeQuery(id+"F0.imprint","IMPRINT",FACE,{"disambiguationData":[TD([[makeQuery(id+"F0.imprint","IMPRINT",EDGE,{"derivedFrom":subQ7}),-1.0]])]});}
            extrude(context, id + "F4", {"entities" : qUnion([Q0]), "depth" : 10 * mm, "offsetDistance" : 25 * mm});
        }
        {
            var Q0;
            {var subQ0=sQuery(id+"F0.wireOp",EDGE,"E258");var subQ1=sQuery(id+"F0.wireOp",EDGE,"E120");var subQ2=makeQuery(id+"F0.imprint","INTERSECT",VERTEX,{"derivedFrom":[subQ1,subQ0]});Q0=makeQuery(id+"F0.imprint","IMPRINT",FACE,{"disambiguationData":[TD([[makeQuery(id+"F0.imprint","IMPRINT",EDGE,{"disambiguationData":[TD([[subQ2,-1.0]])],"derivedFrom":subQ1}),1.0]])]});}
            extrude(context, id + "F5", {"entities" : qUnion([Q0]), "depth" : 5 * mm, "offsetDistance" : 25 * mm});
        }
        {
            var Q0;
            Q0=makeQuery(id+"F1.opExtrude","CAP_FACE",FACE,{"disambiguationData":[OSD([sQuery(id+"F0.wireOp",EDGE,"E146"),sQuery(id+"F0.wireOp",EDGE,"E147"),sQuery(id+"F0.wireOp",EDGE,"E148"),sQuery(id+"F0.wireOp",EDGE,"E149"),sQuery(id+"F0.wireOp",EDGE,"E151"),sQuery(id+"F0.wireOp",EDGE,"E252"),sQuery(id+"F0.wireOp",EDGE,"E253")])],"isStart":false});
            var sketch = newSketch(context, id + "F6", { "sketchPlane" : qUnion([Q0])});
            skText(sketch, "E260", { "text": "F", "fontName": "OpenSans-Bold.ttf"});
            skText(sketch, "E261", { "text": "G", "fontName": "OpenSans-Regular.ttf"});
            skCircle(sketch, "E262", {"center": v(-37.24, 8.14) * mm, "radius": 1.64 * mm});
            const initialGuessF6  = {"E260": [-0.0571, -0.00576, 1, 0, 0.01112], "E261": [-0.04697, -0.00576, 1, 0, 0.01112]};
            skSetInitialGuess(sketch, initialGuessF6);
            skSolve(sketch);
        }
        {
            var Q0;
            Q0=qSketchRegion(id+"F6",true);
            extrude(context, id + "F7", {"entities" : qUnion([Q0]), "operationType" : NewBodyOperationType.ADD, "depth" : 3 * mm, "offsetDistance" : 25 * mm});
        }
        {
            var Q0;
            Q0=qCreatedBy(makeId("Top.planeOp"),FACE);
            var sketch = newSketch(context, id + "F8", { "sketchPlane" : qUnion([Q0])});
            skCircle(sketch, "E263", {"center": v(-44.54, -0.29) * mm, "radius": 25.65 * mm});
            skPoint(sketch, "E263.first.point", {"position": v(-69.58, -5.9) * mm});
            skPoint(sketch, "E263.second.point", {"position": v(-20.3, -8.69) * mm});
            skPoint(sketch, "E263.third.point", {"position": v(-46.85, 25.26) * mm});
            skSolve(sketch);
        }
        {
            var Q0;
            Q0=makeQuery(id+"F8.imprint","IMPRINT",FACE,{"disambiguationData":[TD([[makeQuery(id+"F8.imprint","IMPRINT",EDGE,{"derivedFrom":sQuery(id+"F8.wireOp",EDGE,"E263")}),1.0]])]});
            extrude(context, id + "F9", {"entities" : qUnion([Q0]), "depth" : 2 * mm, "offsetDistance" : 25 * mm});
        }
        {
            var Q0;
            Q0=makeQuery(id+"F5.opExtrude","CAP_EDGE",EDGE,{"disambiguationData":[OSD([sQuery(id+"F0.wireOp",EDGE,"E259")])],"isStart":false});
            var Q1;
            Q1=makeQuery(id+"F5.opExtrude","CAP_EDGE",EDGE,{"disambiguationData":[OSD([sQuery(id+"F0.wireOp",EDGE,"E258")])],"isStart":false});
            var Q2;
            Q2=makeQuery(id+"F5.opExtrude","CAP_EDGE",EDGE,{"disambiguationData":[OSD([sQuery(id+"F0.wireOp",EDGE,"E258")])],"isStart":true});
            var Q3;
            Q3=makeQuery(id+"F5.opExtrude","CAP_EDGE",EDGE,{"disambiguationData":[OSD([sQuery(id+"F0.wireOp",EDGE,"E259")])],"isStart":true});
            fillet(context, id + "F10", {"entities" : qUnion([Q0, Q1, Q2, Q3]), "radius" : 1 * mm, "tangentPropagation" : true, "allowEdgeOverflow" : false});
        }
    });
